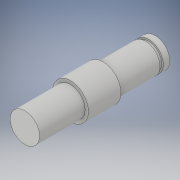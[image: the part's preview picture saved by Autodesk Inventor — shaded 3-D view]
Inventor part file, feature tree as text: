
AUTODESK INVENTOR PART (.ipt)
format: ipt  version: 2019 (Build 230136000, 136)  size: 118,784 bytes
history: native  units: mm
features: extrude x3, sketch x3, plane x2
ambient origin geometry x8: Origin, YZ Plane, XZ Plane, XY Plane, X Axis, Y Axis, Z Axis, Center Point
bodies: Body1 (feature_tree)
feature tree (8):
  extrude  "擠出2"  Depth=9.0mm
  plane  "工作平面3"
  extrude  "擠出5"  Depth=40.0mm TaperAngle=0.0deg
  plane  "工作平面4"
  extrude  "擠出6"  [1 undecoded]
  sketch  "草圖2"
  sketch  "草圖5"
  sketch  "草圖6"
note: 1 required parameter value undecoded (feature->parameter linkage not recoverable at this tier; creation-order binding heuristic only, values carry confidence <= 0.55)
